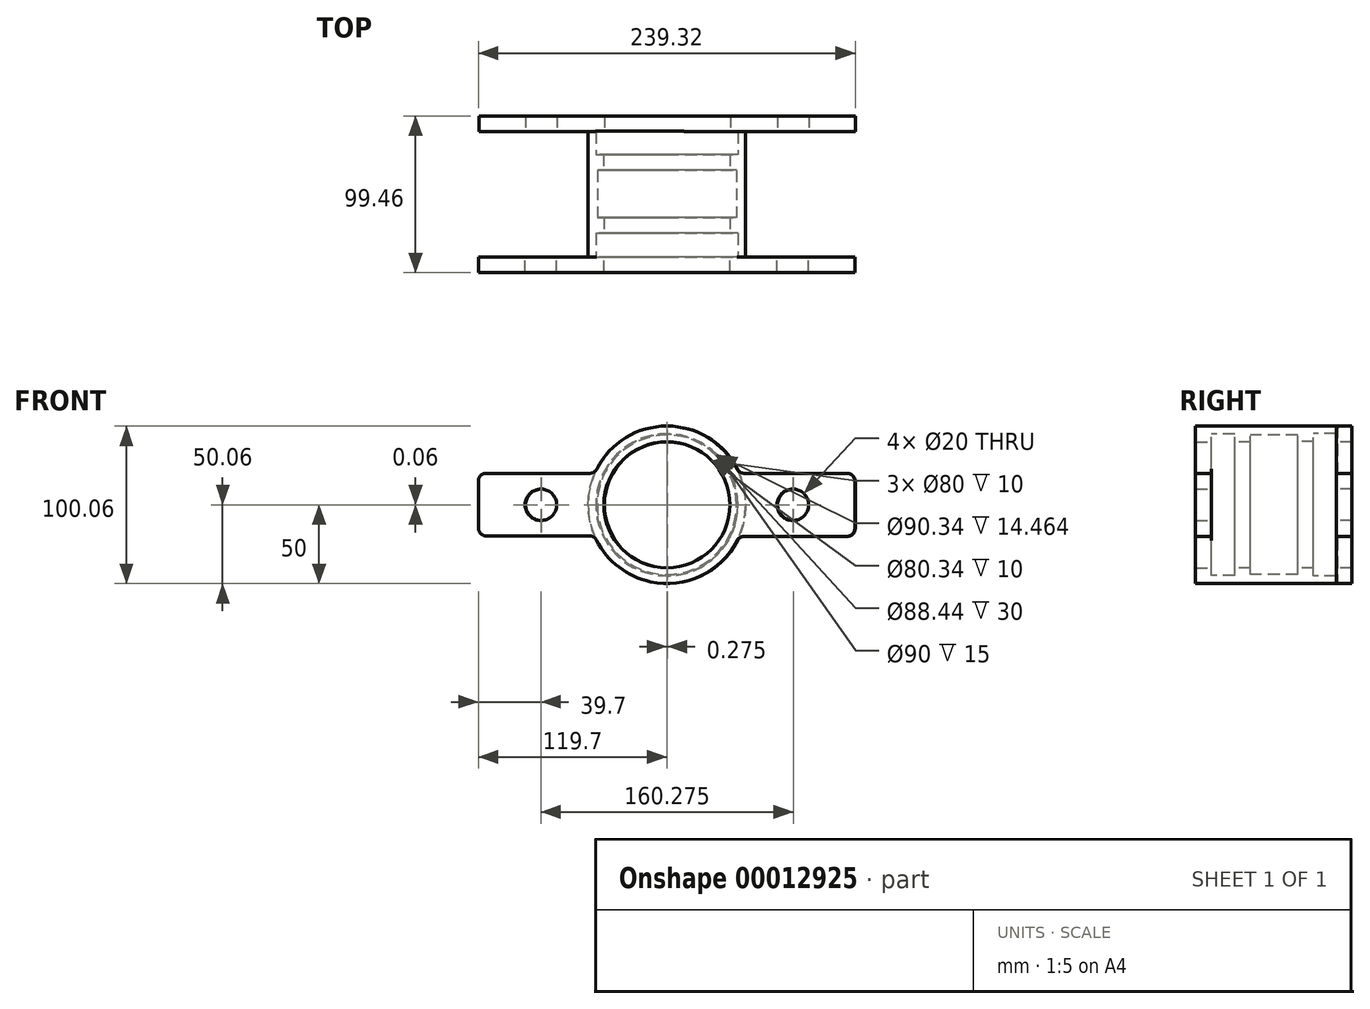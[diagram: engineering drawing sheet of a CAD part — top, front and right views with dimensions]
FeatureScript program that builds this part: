
annotation { "Feature Type Name" : "Feature", "Feature Type Description" : "" }
export const myFeature = defineFeature(function(context is Context, id is Id, definition is map)
    precondition{}
    {
        {
            var Q0;
            Q0=qCreatedBy(makeId("Right.planeOp"),FACE);
            var sketch = newSketch(context, id + "F0", { "sketchPlane" : qUnion([Q0])});
            skLineSegment(sketch, "E0", {"start": v(-51.46, 0) * mm, "end": v(-51.46, -50) * mm});
            skLineSegment(sketch, "E1", {"start": v(-51.46, -50) * mm, "end": v(28.54, -50) * mm});
            skLineSegment(sketch, "E2", {"start": v(28.54, -50) * mm, "end": v(28.54, 0) * mm});
            skLineSegment(sketch, "E3", {"start": v(-51.46, -45) * mm, "end": v(-36.46, -45) * mm});
            skLineSegment(sketch, "E4", {"start": v(-36.46, -45) * mm, "end": v(-36.46, -40) * mm});
            skLineSegment(sketch, "E5", {"start": v(-36.46, -40) * mm, "end": v(-26.46, -40) * mm});
            skLineSegment(sketch, "E6", {"start": v(-26.46, -40) * mm, "end": v(-26.46, -44.22) * mm});
            skLineSegment(sketch, "E7", {"start": v(-26.46, -44.22) * mm, "end": v(3.54, -44.22) * mm});
            skLineSegment(sketch, "E8", {"start": v(3.54, -44.22) * mm, "end": v(3.54, -40.17) * mm});
            skLineSegment(sketch, "E9", {"start": v(3.54, -40.17) * mm, "end": v(13.54, -40.17) * mm});
            skLineSegment(sketch, "E10", {"start": v(13.54, -40.17) * mm, "end": v(13.54, -45.17) * mm});
            skLineSegment(sketch, "E11", {"start": v(13.54, -45.17) * mm, "end": v(28.54, -45.17) * mm});
            skLineSegment(sketch, "E12", {"start": v(-51.46, 0) * mm, "end": v(28.54, 0) * mm});
            skSolve(sketch);
        }
        {
            var Q0;
            {var subQ3=sQuery(id+"F0.wireOp",EDGE,"E1");Q0=makeQuery(id+"F0.imprint","IMPRINT",FACE,{"disambiguationData":[TD([[makeQuery(id+"F0.imprint","IMPRINT",EDGE,{"derivedFrom":subQ3}),1.0]])]});}
            var Q1;
            Q1=sQuery(id+"F0.wireOp",EDGE,"E12");
            revolve(context, id + "F1", {"entities" : qUnion([Q0]), "axis" : qUnion([Q1]), "revolveType" : RevolveType.FULL});
        }
        {
            var Q0;
            Q0=qCreatedBy(makeId("Front.planeOp"),FACE);
            var Q1;
            Q1 = qBodyType(qCreatedBy(id + "F3" ,EDGE), BodyType.WIRE);
            cPlane(context, id + "F2", {"entities" : qUnion([Q0, Q1]), "cplaneType" : CPlaneType.OFFSET, "offset" : 51.46 * mm, "width" : 150 * mm, "height" : 150 * mm});
        }
        {
            var Q0;
            Q0=qCreatedBy(id+"F2.planeOp",FACE);
            var sketch = newSketch(context, id + "F3", { "sketchPlane" : qUnion([Q0])});
            skLineSegment(sketch, "E13", {"start": v(-114.72, 0) * mm, "end": v(104.4, 0) * mm, "construction": true});
            skCircle(sketch, "E14", {"center": v(-80, 0) * mm, "radius": 10 * mm});
            skCircle(sketch, "E15", {"center": v(80, 0) * mm, "radius": 10 * mm});
            skLineSegment(sketch, "E16", {"start": v(-119.7, 15) * mm, "end": v(-119.7, -14.75) * mm});
            skLineSegment(sketch, "E17", {"start": v(48.99, 20) * mm, "end": v(114.35, 20) * mm});
            skLineSegment(sketch, "E18", {"start": v(119.35, 15) * mm, "end": v(119.35, -15) * mm});
            skLineSegment(sketch, "E19", {"start": v(114.35, -20) * mm, "end": v(48.99, -20) * mm});
            skPoint(sketch, "E20.visualSharp", {"position": v(-119.7, 20.25) * mm});
            skArc(sketch, "E20.filletArc", {"start": v(-114.7, 20) * mm, "mid": v(-118.24, 18.54) * mm, "end": v(-119.7, 15) * mm});
            skPoint(sketch, "E21.visualSharp", {"position": v(-119.7, -19.75) * mm});
            skArc(sketch, "E21.filletArc", {"start": v(-119.7, -14.75) * mm, "mid": v(-118.24, -18.28) * mm, "end": v(-114.7, -19.75) * mm});
            skPoint(sketch, "E22.visualSharp", {"position": v(119.35, 20) * mm});
            skArc(sketch, "E22.filletArc", {"start": v(119.35, 15) * mm, "mid": v(117.88, 18.54) * mm, "end": v(114.35, 20) * mm});
            skPoint(sketch, "E23.visualSharp", {"position": v(119.35, -20) * mm});
            skArc(sketch, "E23.filletArc", {"start": v(114.35, -20) * mm, "mid": v(117.88, -18.54) * mm, "end": v(119.35, -15) * mm});
            skArc(sketch, "E24", {"start": v(44.54, 22.73) * mm, "mid": v(0, 50) * mm, "end": v(-44.54, 22.73) * mm});
            skLineSegment(sketch, "E25", {"start": v(-114.7, 20) * mm, "end": v(-48.99, 20) * mm});
            skPoint(sketch, "E26.visualSharp", {"position": v(45.83, 20) * mm});
            skArc(sketch, "E26.filletArc", {"start": v(44.54, 22.73) * mm, "mid": v(46.38, 20.74) * mm, "end": v(48.99, 20) * mm});
            skPoint(sketch, "E27.visualSharp", {"position": v(45.83, -20) * mm});
            skArc(sketch, "E27.filletArc", {"start": v(48.99, -20) * mm, "mid": v(46.38, -20.74) * mm, "end": v(44.54, -22.73) * mm});
            skArc(sketch, "E28.trimOffspring", {"start": v(-44.65, -22.5) * mm, "mid": v(-0.13, -50) * mm, "end": v(44.54, -22.73) * mm});
            skLineSegment(sketch, "E29", {"start": v(-114.7, -19.75) * mm, "end": v(-49.12, -19.75) * mm});
            skPoint(sketch, "E30.visualSharp", {"position": v(-45.83, 20) * mm});
            skArc(sketch, "E30.filletArc", {"start": v(-48.99, 20) * mm, "mid": v(-46.38, 20.74) * mm, "end": v(-44.54, 22.73) * mm});
            skPoint(sketch, "E31.visualSharp", {"position": v(-45.93, -19.75) * mm});
            skArc(sketch, "E31.filletArc", {"start": v(-44.65, -22.5) * mm, "mid": v(-46.5, -20.5) * mm, "end": v(-49.12, -19.75) * mm});
            skCircle(sketch, "E32", {"center": v(0, 0) * mm, "radius": 40 * mm});
            skSolve(sketch);
        }
        {
            var Q0;
            Q0=makeQuery(id+"F3.imprint","IMPRINT",FACE,{"disambiguationData":[TD([[makeQuery(id+"F3.imprint","IMPRINT",EDGE,{"derivedFrom":sQuery(id+"F3.wireOp",EDGE,"E14")}),-1.0]])]});
            extrude(context, id + "F4", {"entities" : qUnion([Q0]), "operationType" : NewBodyOperationType.ADD, "depth" : 10 * mm});
        }
        {
            var Q0;
            Q0=qCreatedBy(makeId("Front.planeOp"),FACE);
            cPlane(context, id + "F5", {"entities" : qUnion([Q0]), "cplaneType" : CPlaneType.OFFSET, "offset" : 28 * mm, "oppositeDirection" : true, "width" : 150 * mm, "height" : 150 * mm});
        }
        {
            var Q0;
            Q0=qCreatedBy(id+"F5.planeOp",FACE);
            var sketch = newSketch(context, id + "F6", { "sketchPlane" : qUnion([Q0])});
            skLineSegment(sketch, "E33", {"start": v(-114.45, -0.06) * mm, "end": v(104.68, -0.06) * mm, "construction": true});
            skCircle(sketch, "E34", {"center": v(-79.73, -0.06) * mm, "radius": 10 * mm});
            skCircle(sketch, "E35", {"center": v(80.27, -0.06) * mm, "radius": 10 * mm});
            skLineSegment(sketch, "E36", {"start": v(-119.43, 14.94) * mm, "end": v(-119.43, -14.8) * mm});
            skLineSegment(sketch, "E37", {"start": v(49.26, 19.94) * mm, "end": v(114.62, 19.94) * mm});
            skLineSegment(sketch, "E38", {"start": v(119.62, 14.94) * mm, "end": v(119.62, -15.06) * mm});
            skLineSegment(sketch, "E39", {"start": v(114.62, -20.06) * mm, "end": v(49.26, -20.06) * mm});
            skPoint(sketch, "E40.visualSharp", {"position": v(-119.43, 20.2) * mm});
            skArc(sketch, "E40.filletArc", {"start": v(-114.43, 19.94) * mm, "mid": v(-117.97, 18.48) * mm, "end": v(-119.43, 14.94) * mm});
            skPoint(sketch, "E41.visualSharp", {"position": v(-119.43, -19.8) * mm});
            skArc(sketch, "E41.filletArc", {"start": v(-119.43, -14.8) * mm, "mid": v(-117.97, -18.34) * mm, "end": v(-114.43, -19.8) * mm});
            skPoint(sketch, "E42.visualSharp", {"position": v(119.62, 19.94) * mm});
            skArc(sketch, "E42.filletArc", {"start": v(119.62, 14.94) * mm, "mid": v(118.16, 18.48) * mm, "end": v(114.62, 19.94) * mm});
            skPoint(sketch, "E43.visualSharp", {"position": v(119.62, -20.06) * mm});
            skArc(sketch, "E43.filletArc", {"start": v(114.62, -20.06) * mm, "mid": v(118.16, -18.6) * mm, "end": v(119.62, -15.06) * mm});
            skArc(sketch, "E44", {"start": v(44.81, 22.67) * mm, "mid": v(0.27, 49.94) * mm, "end": v(-44.26, 22.67) * mm});
            skLineSegment(sketch, "E45", {"start": v(-114.43, 19.94) * mm, "end": v(-48.72, 19.94) * mm});
            skPoint(sketch, "E46.visualSharp", {"position": v(46.1, 19.94) * mm});
            skArc(sketch, "E46.filletArc", {"start": v(44.81, 22.67) * mm, "mid": v(46.65, 20.68) * mm, "end": v(49.26, 19.94) * mm});
            skPoint(sketch, "E47.visualSharp", {"position": v(46.1, -20.06) * mm});
            skArc(sketch, "E47.filletArc", {"start": v(49.26, -20.06) * mm, "mid": v(46.65, -20.8) * mm, "end": v(44.81, -22.79) * mm});
            skArc(sketch, "E48.trimOffspring", {"start": v(-44.38, -22.56) * mm, "mid": v(0.15, -50.06) * mm, "end": v(44.81, -22.79) * mm});
            skLineSegment(sketch, "E49", {"start": v(-114.43, -19.8) * mm, "end": v(-48.84, -19.8) * mm});
            skPoint(sketch, "E50.visualSharp", {"position": v(-45.55, 19.94) * mm});
            skArc(sketch, "E50.filletArc", {"start": v(-48.72, 19.94) * mm, "mid": v(-46.1, 20.68) * mm, "end": v(-44.26, 22.67) * mm});
            skPoint(sketch, "E51.visualSharp", {"position": v(-45.66, -19.8) * mm});
            skArc(sketch, "E51.filletArc", {"start": v(-44.38, -22.56) * mm, "mid": v(-46.22, -20.55) * mm, "end": v(-48.84, -19.8) * mm});
            skCircle(sketch, "E52", {"center": v(0.27, -0.06) * mm, "radius": 40 * mm});
            skSolve(sketch);
        }
        {
            var Q0;
            Q0=makeQuery(id+"F6.imprint","IMPRINT",FACE,{"disambiguationData":[TD([[makeQuery(id+"F6.imprint","IMPRINT",EDGE,{"derivedFrom":sQuery(id+"F6.wireOp",EDGE,"E34")}),-1.0]])]});
            extrude(context, id + "F7", {"entities" : qUnion([Q0]), "operationType" : NewBodyOperationType.ADD, "oppositeDirection" : true, "depth" : 10 * mm});
        }
    });
